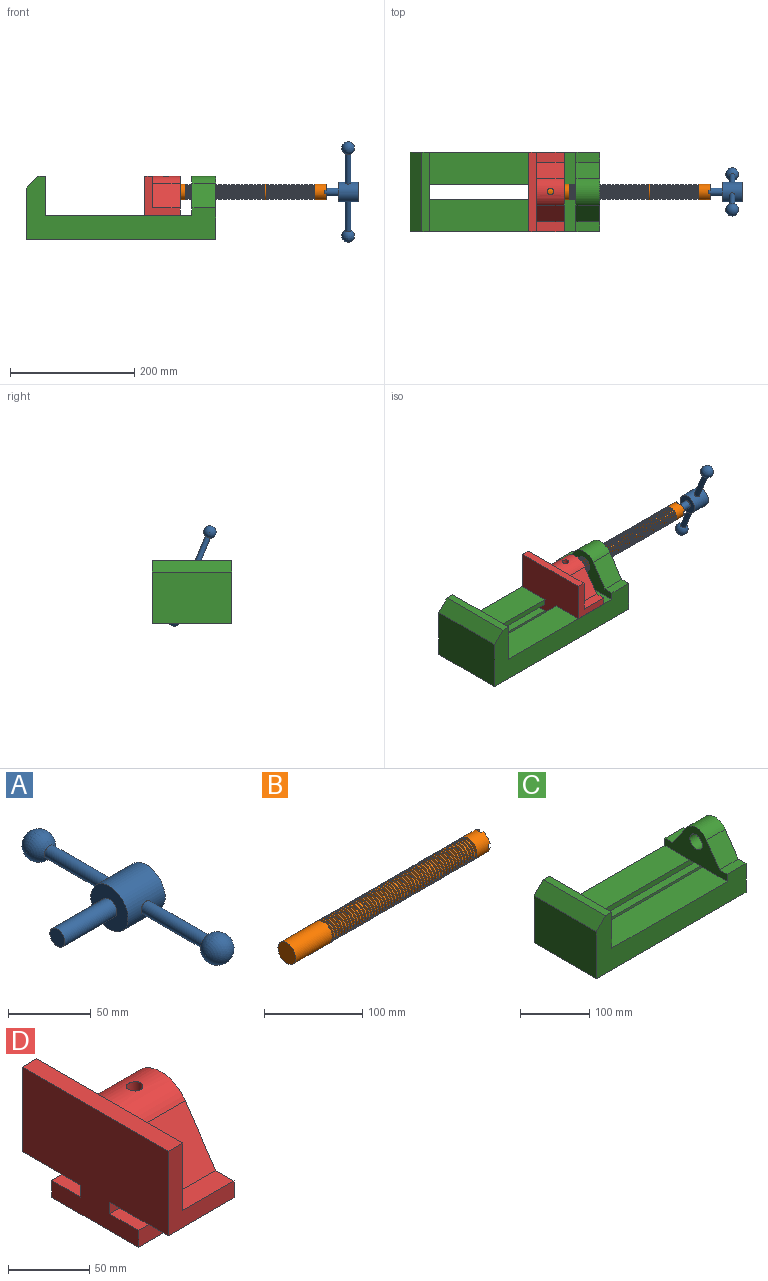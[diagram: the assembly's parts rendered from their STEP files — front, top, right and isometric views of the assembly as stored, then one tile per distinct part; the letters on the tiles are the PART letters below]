
ASSEMBLY  parts=4 mates=3
PART A: 13 faces, bbox 76.2x172.7x31.8 mm
  f0: cylinder r=4.45mm len=51.82mm, axis (0,1,0), area 1438.5mm2, adj f1,f8
  f1: cylinder r=15.88mm len=31.75mm, axis (-1,0,0), area 3041.6mm2, adj f0,f4,f5,f6
  f2: cylinder r=6.35mm len=44.45mm, axis (-1,0,0), area 1773.5mm2, adj f3,f5
  f3: plane 12.7x12.7mm, normal (-1,0,0), area 126.7mm2, adj f2
  f4: plane 31.75x31.75mm, normal (1,0,0), area 791.7mm2, adj f1
  f5: plane 31.75x31.75mm, normal (-1,0,0), area 665.1mm2, adj f1,f2
  f6: cylinder r=4.45mm len=51.82mm, axis (0,1,0), area 1438.5mm2, adj f1,f7
  f7: sphere r=10.16mm, area 1231.8mm2, adj f6
  f8: sphere r=10.16mm, area 1231.8mm2, adj f0
  f9: sphere r=4.45mm, area 124.1mm2, adj f10
  f10: plane 8.89x8.89mm, normal (0,-1,0), area 62.1mm2, adj f9
  f11: sphere r=4.45mm, area 124.1mm2, adj f12
  f12: plane 8.89x8.89mm, normal (0,1,0), area 62.1mm2, adj f11
PART B: 220 faces, bbox 279.4x25.4x25.4 mm
  f0: cylinder r=12.7mm len=25.4mm, axis (-1,0,0), area 1468.2mm2, adj f1,f2,f3,f4,f7,f208,f209,f210
  f1: plane 9.9x9.9mm, normal (1,0,0), area 62.3mm2, adj f0,f5,f215,f217
  f2: plane 9.9x9.9mm, normal (1,0,0), area 62.3mm2, adj f0,f5,f209,f218
  f3: plane 9.9x9.9mm, normal (1,0,0), area 62.3mm2, adj f0,f5,f211,f214
  f4: plane 9.9x9.9mm, normal (1,0,0), area 62.3mm2, adj f0,f5,f208,f212
  f5: cylinder r=6.35mm len=25.4mm, axis (1,0,0), area 960.3mm2, adj f1,f2,f3,f4,f6,f208,f209,f210
  f6: plane 12.7x12.7mm, normal (1,0,0), area 126.7mm2, adj f5
  f7: cone r=12.7mm half-angle=76deg, axis (1,0,0), area 188mm2, adj f0,f9
  f8: cone r=12.7mm half-angle=76deg, axis (-1,0,0), area 188mm2, adj f9,f10
  f9: cylinder r=10.16mm len=20.32mm, axis (1,0,0), area 81.1mm2, adj f7,f8
  f10: cylinder r=12.7mm len=25.4mm, axis (-1,0,0), area 131.7mm2, adj f8,f11
  f11: cone r=12.7mm half-angle=76deg, axis (1,0,0), area 188mm2, adj f10,f13
  f12: cone r=12.7mm half-angle=76deg, axis (-1,0,0), area 188mm2, adj f13,f14
  f13: cylinder r=10.16mm len=20.32mm, axis (1,0,0), area 81.1mm2, adj f11,f12
  f14: cylinder r=12.7mm len=25.4mm, axis (-1,0,0), area 131.7mm2, adj f12,f15
  f15: cone r=12.7mm half-angle=76deg, axis (1,0,0), area 188mm2, adj f14,f17
  f16: cone r=12.7mm half-angle=76deg, axis (-1,0,0), area 188mm2, adj f17,f18
  f17: cylinder r=10.16mm len=20.32mm, axis (1,0,0), area 81.1mm2, adj f15,f16
  f18: cylinder r=12.7mm len=25.4mm, axis (-1,0,0), area 131.7mm2, adj f16,f19
  f19: cone r=12.7mm half-angle=76deg, axis (1,0,0), area 188mm2, adj f18,f21
  f20: cone r=12.7mm half-angle=76deg, axis (-1,0,0), area 188mm2, adj f21,f22
  f21: cylinder r=10.16mm len=20.32mm, axis (1,0,0), area 81.1mm2, adj f19,f20
  f22: cylinder r=12.7mm len=25.4mm, axis (-1,0,0), area 131.7mm2, adj f20,f23
  f23: cone r=12.7mm half-angle=76deg, axis (1,0,0), area 188mm2, adj f22,f25
  f24: cone r=12.7mm half-angle=76deg, axis (-1,0,0), area 188mm2, adj f25,f26
  f25: cylinder r=10.16mm len=20.32mm, axis (1,0,0), area 81.1mm2, adj f23,f24
  f26: cylinder r=12.7mm len=25.4mm, axis (-1,0,0), area 131.7mm2, adj f24,f27
  f27: cone r=12.7mm half-angle=76deg, axis (1,0,0), area 188mm2, adj f26,f29
  f28: cone r=12.7mm half-angle=76deg, axis (-1,0,0), area 188mm2, adj f29,f30
  f29: cylinder r=10.16mm len=20.32mm, axis (1,0,0), area 81.1mm2, adj f27,f28
  f30: cylinder r=12.7mm len=25.4mm, axis (-1,0,0), area 131.7mm2, adj f28,f31
  f31: cone r=12.7mm half-angle=76deg, axis (1,0,0), area 188mm2, adj f30,f33
  f32: cone r=12.7mm half-angle=76deg, axis (-1,0,0), area 188mm2, adj f33,f34
  f33: cylinder r=10.16mm len=20.32mm, axis (1,0,0), area 81.1mm2, adj f31,f32
  f34: cylinder r=12.7mm len=25.4mm, axis (-1,0,0), area 131.7mm2, adj f32,f35
  f35: cone r=12.7mm half-angle=76deg, axis (1,0,0), area 188mm2, adj f34,f37
  f36: cone r=12.7mm half-angle=76deg, axis (-1,0,0), area 188mm2, adj f37,f38
  f37: cylinder r=10.16mm len=20.32mm, axis (1,0,0), area 81.1mm2, adj f35,f36
  f38: cylinder r=12.7mm len=25.4mm, axis (-1,0,0), area 131.7mm2, adj f36,f39
  f39: cone r=12.7mm half-angle=76deg, axis (1,0,0), area 188mm2, adj f38,f41
  f40: cone r=12.7mm half-angle=76deg, axis (-1,0,0), area 188mm2, adj f41,f42
  f41: cylinder r=10.16mm len=20.32mm, axis (1,0,0), area 81.1mm2, adj f39,f40
  f42: cylinder r=12.7mm len=25.4mm, axis (-1,0,0), area 131.7mm2, adj f40,f43
  f43: cone r=12.7mm half-angle=76deg, axis (1,0,0), area 188mm2, adj f42,f45
  f44: cone r=12.7mm half-angle=76deg, axis (-1,0,0), area 188mm2, adj f45,f46
  f45: cylinder r=10.16mm len=20.32mm, axis (1,0,0), area 81.1mm2, adj f43,f44
  f46: cylinder r=12.7mm len=25.4mm, axis (-1,0,0), area 131.7mm2, adj f44,f47
  f47: cone r=12.7mm half-angle=76deg, axis (1,0,0), area 188mm2, adj f46,f49
  f48: cone r=12.7mm half-angle=76deg, axis (-1,0,0), area 188mm2, adj f49,f50
  f49: cylinder r=10.16mm len=20.32mm, axis (1,0,0), area 81.1mm2, adj f47,f48
  f50: cylinder r=12.7mm len=25.4mm, axis (-1,0,0), area 131.7mm2, adj f48,f51
  f51: cone r=12.7mm half-angle=76deg, axis (1,0,0), area 188mm2, adj f50,f53
  f52: cone r=12.7mm half-angle=76deg, axis (-1,0,0), area 188mm2, adj f53,f54
  f53: cylinder r=10.16mm len=20.32mm, axis (1,0,0), area 81.1mm2, adj f51,f52
  f54: cylinder r=12.7mm len=25.4mm, axis (-1,0,0), area 131.7mm2, adj f52,f55
  f55: cone r=12.7mm half-angle=76deg, axis (1,0,0), area 188mm2, adj f54,f57
  f56: cone r=12.7mm half-angle=76deg, axis (-1,0,0), area 188mm2, adj f57,f58
  f57: cylinder r=10.16mm len=20.32mm, axis (1,0,0), area 81.1mm2, adj f55,f56
  f58: cylinder r=12.7mm len=25.4mm, axis (-1,0,0), area 131.7mm2, adj f56,f59
  f59: cone r=12.7mm half-angle=76deg, axis (1,0,0), area 188mm2, adj f58,f61
  f60: cone r=12.7mm half-angle=76deg, axis (-1,0,0), area 188mm2, adj f61,f62
  f61: cylinder r=10.16mm len=20.32mm, axis (1,0,0), area 81.1mm2, adj f59,f60
  f62: cylinder r=12.7mm len=25.4mm, axis (-1,0,0), area 131.7mm2, adj f60,f63
  f63: cone r=12.7mm half-angle=76deg, axis (1,0,0), area 188mm2, adj f62,f65
  f64: cone r=12.7mm half-angle=76deg, axis (-1,0,0), area 188mm2, adj f65,f66
  f65: cylinder r=10.16mm len=20.32mm, axis (1,0,0), area 81.1mm2, adj f63,f64
  f66: cylinder r=12.7mm len=25.4mm, axis (-1,0,0), area 131.7mm2, adj f64,f67
  f67: cone r=12.7mm half-angle=76deg, axis (1,0,0), area 188mm2, adj f66,f69
  f68: cone r=12.7mm half-angle=76deg, axis (-1,0,0), area 188mm2, adj f69,f70
  f69: cylinder r=10.16mm len=20.32mm, axis (1,0,0), area 81.1mm2, adj f67,f68
  f70: cylinder r=12.7mm len=25.4mm, axis (-1,0,0), area 131.7mm2, adj f68,f71
  f71: cone r=12.7mm half-angle=76deg, axis (1,0,0), area 188mm2, adj f70,f73
  f72: cone r=12.7mm half-angle=76deg, axis (-1,0,0), area 188mm2, adj f73,f74
  f73: cylinder r=10.16mm len=20.32mm, axis (1,0,0), area 81.1mm2, adj f71,f72
  f74: cylinder r=12.7mm len=25.4mm, axis (-1,0,0), area 131.7mm2, adj f72,f75
  f75: cone r=12.7mm half-angle=76deg, axis (1,0,0), area 188mm2, adj f74,f77
  f76: cone r=12.7mm half-angle=76deg, axis (-1,0,0), area 188mm2, adj f77,f78
  f77: cylinder r=10.16mm len=20.32mm, axis (1,0,0), area 81.1mm2, adj f75,f76
  f78: cylinder r=12.7mm len=25.4mm, axis (-1,0,0), area 131.7mm2, adj f76,f79
  f79: cone r=12.7mm half-angle=76deg, axis (1,0,0), area 188mm2, adj f78,f81
  f80: cone r=12.7mm half-angle=76deg, axis (-1,0,0), area 188mm2, adj f81,f82
  f81: cylinder r=10.16mm len=20.32mm, axis (1,0,0), area 81.1mm2, adj f79,f80
  f82: cylinder r=12.7mm len=25.4mm, axis (-1,0,0), area 131.7mm2, adj f80,f83
  f83: cone r=12.7mm half-angle=76deg, axis (1,0,0), area 188mm2, adj f82,f85
  f84: cone r=12.7mm half-angle=76deg, axis (-1,0,0), area 188mm2, adj f85,f86
  f85: cylinder r=10.16mm len=20.32mm, axis (1,0,0), area 81.1mm2, adj f83,f84
  f86: cylinder r=12.7mm len=25.4mm, axis (-1,0,0), area 131.7mm2, adj f84,f87
  f87: cone r=12.7mm half-angle=76deg, axis (1,0,0), area 188mm2, adj f86,f89
  f88: cone r=12.7mm half-angle=76deg, axis (-1,0,0), area 188mm2, adj f89,f90
  f89: cylinder r=10.16mm len=20.32mm, axis (1,0,0), area 81.1mm2, adj f87,f88
  f90: cylinder r=12.7mm len=25.4mm, axis (-1,0,0), area 131.7mm2, adj f88,f91
  f91: cone r=12.7mm half-angle=76deg, axis (1,0,0), area 188mm2, adj f90,f93
  f92: cone r=12.7mm half-angle=76deg, axis (-1,0,0), area 188mm2, adj f93,f94
  f93: cylinder r=10.16mm len=20.32mm, axis (1,0,0), area 81.1mm2, adj f91,f92
  f94: cylinder r=12.7mm len=25.4mm, axis (-1,0,0), area 131.7mm2, adj f92,f95
  f95: cone r=12.7mm half-angle=76deg, axis (1,0,0), area 188mm2, adj f94,f97
  f96: cone r=12.7mm half-angle=76deg, axis (-1,0,0), area 188mm2, adj f97,f98
  f97: cylinder r=10.16mm len=20.32mm, axis (1,0,0), area 81.1mm2, adj f95,f96
  f98: cylinder r=12.7mm len=25.4mm, axis (-1,0,0), area 131.7mm2, adj f96,f99
  f99: cone r=12.7mm half-angle=76deg, axis (1,0,0), area 188mm2, adj f98,f101
  f100: cone r=12.7mm half-angle=76deg, axis (-1,0,0), area 188mm2, adj f101,f102
  f101: cylinder r=10.16mm len=20.32mm, axis (1,0,0), area 81.1mm2, adj f99,f100
  f102: cylinder r=12.7mm len=25.4mm, axis (-1,0,0), area 131.7mm2, adj f100,f103
  f103: cone r=12.7mm half-angle=76deg, axis (1,0,0), area 188mm2, adj f102,f105
  f104: cone r=12.7mm half-angle=76deg, axis (-1,0,0), area 188mm2, adj f105,f106
  f105: cylinder r=10.16mm len=20.32mm, axis (1,0,0), area 81.1mm2, adj f103,f104
  f106: cylinder r=12.7mm len=25.4mm, axis (-1,0,0), area 131.7mm2, adj f104,f107
  f107: cone r=12.7mm half-angle=76deg, axis (1,0,0), area 188mm2, adj f106,f109
  f108: cone r=12.7mm half-angle=76deg, axis (-1,0,0), area 188mm2, adj f109,f110
  f109: cylinder r=10.16mm len=20.32mm, axis (1,0,0), area 81.1mm2, adj f107,f108
  f110: cylinder r=12.7mm len=25.4mm, axis (-1,0,0), area 131.7mm2, adj f108,f111
  f111: cone r=12.7mm half-angle=76deg, axis (1,0,0), area 188mm2, adj f110,f113
  f112: cone r=12.7mm half-angle=76deg, axis (-1,0,0), area 188mm2, adj f113,f114
  f113: cylinder r=10.16mm len=20.32mm, axis (1,0,0), area 81.1mm2, adj f111,f112
  f114: cylinder r=12.7mm len=25.4mm, axis (-1,0,0), area 131.7mm2, adj f112,f115
  f115: cone r=12.7mm half-angle=76deg, axis (1,0,0), area 188mm2, adj f114,f117
  f116: cone r=12.7mm half-angle=76deg, axis (-1,0,0), area 188mm2, adj f117,f118
  f117: cylinder r=10.16mm len=20.32mm, axis (1,0,0), area 81.1mm2, adj f115,f116
  f118: cylinder r=12.7mm len=25.4mm, axis (-1,0,0), area 131.7mm2, adj f116,f119
  f119: cone r=12.7mm half-angle=76deg, axis (1,0,0), area 188mm2, adj f118,f121
  f120: cone r=12.7mm half-angle=76deg, axis (-1,0,0), area 188mm2, adj f121,f122
  f121: cylinder r=10.16mm len=20.32mm, axis (1,0,0), area 81.1mm2, adj f119,f120
  f122: cylinder r=12.7mm len=25.4mm, axis (-1,0,0), area 131.7mm2, adj f120,f123
  f123: cone r=12.7mm half-angle=76deg, axis (1,0,0), area 188mm2, adj f122,f125
  f124: cone r=12.7mm half-angle=76deg, axis (-1,0,0), area 188mm2, adj f125,f126
  f125: cylinder r=10.16mm len=20.32mm, axis (1,0,0), area 81.1mm2, adj f123,f124
  f126: cylinder r=12.7mm len=25.4mm, axis (-1,0,0), area 131.7mm2, adj f124,f127
  f127: cone r=12.7mm half-angle=76deg, axis (1,0,0), area 188mm2, adj f126,f129
  f128: cone r=12.7mm half-angle=76deg, axis (-1,0,0), area 188mm2, adj f129,f130
  f129: cylinder r=10.16mm len=20.32mm, axis (1,0,0), area 81.1mm2, adj f127,f128
  f130: cylinder r=12.7mm len=25.4mm, axis (-1,0,0), area 131.7mm2, adj f128,f131
  f131: cone r=12.7mm half-angle=76deg, axis (1,0,0), area 188mm2, adj f130,f133
  f132: cone r=12.7mm half-angle=76deg, axis (-1,0,0), area 188mm2, adj f133,f134
  f133: cylinder r=10.16mm len=20.32mm, axis (1,0,0), area 81.1mm2, adj f131,f132
  f134: cylinder r=12.7mm len=25.4mm, axis (-1,0,0), area 131.7mm2, adj f132,f135
  f135: cone r=12.7mm half-angle=76deg, axis (1,0,0), area 188mm2, adj f134,f137
  f136: cone r=12.7mm half-angle=76deg, axis (-1,0,0), area 188mm2, adj f137,f138
  f137: cylinder r=10.16mm len=20.32mm, axis (1,0,0), area 81.1mm2, adj f135,f136
  f138: cylinder r=12.7mm len=25.4mm, axis (-1,0,0), area 131.7mm2, adj f136,f139
  f139: cone r=12.7mm half-angle=76deg, axis (1,0,0), area 188mm2, adj f138,f141
  f140: cone r=12.7mm half-angle=76deg, axis (-1,0,0), area 188mm2, adj f141,f142
  f141: cylinder r=10.16mm len=20.32mm, axis (1,0,0), area 81.1mm2, adj f139,f140
  f142: cylinder r=12.7mm len=25.4mm, axis (-1,0,0), area 131.7mm2, adj f140,f143
  f143: cone r=12.7mm half-angle=76deg, axis (1,0,0), area 188mm2, adj f142,f145
  f144: cone r=12.7mm half-angle=76deg, axis (-1,0,0), area 188mm2, adj f145,f146
  f145: cylinder r=10.16mm len=20.32mm, axis (1,0,0), area 81.1mm2, adj f143,f144
  f146: cylinder r=12.7mm len=25.4mm, axis (-1,0,0), area 131.7mm2, adj f144,f147
  f147: cone r=12.7mm half-angle=76deg, axis (1,0,0), area 188mm2, adj f146,f149
  f148: cone r=12.7mm half-angle=76deg, axis (-1,0,0), area 188mm2, adj f149,f150
  f149: cylinder r=10.16mm len=20.32mm, axis (1,0,0), area 81.1mm2, adj f147,f148
  f150: cylinder r=12.7mm len=25.4mm, axis (-1,0,0), area 131.7mm2, adj f148,f151
  f151: cone r=12.7mm half-angle=76deg, axis (1,0,0), area 188mm2, adj f150,f153
  f152: cone r=12.7mm half-angle=76deg, axis (-1,0,0), area 188mm2, adj f153,f154
  f153: cylinder r=10.16mm len=20.32mm, axis (1,0,0), area 81.1mm2, adj f151,f152
  f154: cylinder r=12.7mm len=25.4mm, axis (-1,0,0), area 131.7mm2, adj f152,f155
  f155: cone r=12.7mm half-angle=76deg, axis (1,0,0), area 188mm2, adj f154,f157
  f156: cone r=12.7mm half-angle=76deg, axis (-1,0,0), area 188mm2, adj f157,f158
  f157: cylinder r=10.16mm len=20.32mm, axis (1,0,0), area 81.1mm2, adj f155,f156
  f158: cylinder r=12.7mm len=25.4mm, axis (-1,0,0), area 131.7mm2, adj f156,f159
  f159: cone r=12.7mm half-angle=76deg, axis (1,0,0), area 188mm2, adj f158,f161
  f160: cone r=12.7mm half-angle=76deg, axis (-1,0,0), area 188mm2, adj f161,f162
  f161: cylinder r=10.16mm len=20.32mm, axis (1,0,0), area 81.1mm2, adj f159,f160
  f162: cylinder r=12.7mm len=25.4mm, axis (-1,0,0), area 131.7mm2, adj f160,f163
  f163: cone r=12.7mm half-angle=76deg, axis (1,0,0), area 188mm2, adj f162,f165
  f164: cone r=12.7mm half-angle=76deg, axis (-1,0,0), area 188mm2, adj f165,f166
  f165: cylinder r=10.16mm len=20.32mm, axis (1,0,0), area 81.1mm2, adj f163,f164
  f166: cylinder r=12.7mm len=25.4mm, axis (-1,0,0), area 131.7mm2, adj f164,f167
  f167: cone r=12.7mm half-angle=76deg, axis (1,0,0), area 188mm2, adj f166,f169
  f168: cone r=12.7mm half-angle=76deg, axis (-1,0,0), area 188mm2, adj f169,f170
  f169: cylinder r=10.16mm len=20.32mm, axis (1,0,0), area 81.1mm2, adj f167,f168
  f170: cylinder r=12.7mm len=25.4mm, axis (-1,0,0), area 131.7mm2, adj f168,f171
  f171: cone r=12.7mm half-angle=76deg, axis (1,0,0), area 188mm2, adj f170,f173
  f172: cone r=12.7mm half-angle=76deg, axis (-1,0,0), area 188mm2, adj f173,f174
  f173: cylinder r=10.16mm len=20.32mm, axis (1,0,0), area 81.1mm2, adj f171,f172
  f174: cylinder r=12.7mm len=25.4mm, axis (-1,0,0), area 131.7mm2, adj f172,f175
  f175: cone r=12.7mm half-angle=76deg, axis (1,0,0), area 188mm2, adj f174,f177
  f176: cone r=12.7mm half-angle=76deg, axis (-1,0,0), area 188mm2, adj f177,f178
  f177: cylinder r=10.16mm len=20.32mm, axis (1,0,0), area 81.1mm2, adj f175,f176
  f178: cylinder r=12.7mm len=25.4mm, axis (-1,0,0), area 131.7mm2, adj f176,f179
  f179: cone r=12.7mm half-angle=76deg, axis (1,0,0), area 188mm2, adj f178,f181
  f180: cone r=12.7mm half-angle=76deg, axis (-1,0,0), area 188mm2, adj f181,f182
  f181: cylinder r=10.16mm len=20.32mm, axis (1,0,0), area 81.1mm2, adj f179,f180
  f182: cylinder r=12.7mm len=25.4mm, axis (-1,0,0), area 131.7mm2, adj f180,f183
  f183: cone r=12.7mm half-angle=76deg, axis (1,0,0), area 188mm2, adj f182,f185
  f184: cone r=12.7mm half-angle=76deg, axis (-1,0,0), area 188mm2, adj f185,f186
  f185: cylinder r=10.16mm len=20.32mm, axis (1,0,0), area 81.1mm2, adj f183,f184
  f186: cylinder r=12.7mm len=25.4mm, axis (-1,0,0), area 131.7mm2, adj f184,f187
  f187: cone r=12.7mm half-angle=76deg, axis (1,0,0), area 188mm2, adj f186,f189
  f188: cone r=12.7mm half-angle=76deg, axis (-1,0,0), area 188mm2, adj f189,f190
  f189: cylinder r=10.16mm len=20.32mm, axis (1,0,0), area 81.1mm2, adj f187,f188
  f190: cylinder r=12.7mm len=25.4mm, axis (-1,0,0), area 131.7mm2, adj f188,f191
  f191: cone r=12.7mm half-angle=76deg, axis (1,0,0), area 188mm2, adj f190,f193
  f192: cone r=12.7mm half-angle=76deg, axis (-1,0,0), area 188mm2, adj f193,f194
  f193: cylinder r=10.16mm len=20.32mm, axis (1,0,0), area 81.1mm2, adj f191,f192
  f194: cylinder r=12.7mm len=25.4mm, axis (-1,0,0), area 131.7mm2, adj f192,f195
  f195: cone r=12.7mm half-angle=76deg, axis (1,0,0), area 188mm2, adj f194,f197
  f196: cone r=12.7mm half-angle=76deg, axis (-1,0,0), area 188mm2, adj f197,f198
  f197: cylinder r=10.16mm len=20.32mm, axis (1,0,0), area 81.1mm2, adj f195,f196
  f198: cylinder r=12.7mm len=25.4mm, axis (-1,0,0), area 131.7mm2, adj f196,f199
  f199: cone r=12.7mm half-angle=76deg, axis (1,0,0), area 188mm2, adj f198,f201
  f200: cone r=12.7mm half-angle=76deg, axis (-1,0,0), area 188mm2, adj f201,f202
  f201: cylinder r=10.16mm len=20.32mm, axis (1,0,0), area 81.1mm2, adj f199,f200
  f202: cylinder r=12.7mm len=25.4mm, axis (-1,0,0), area 131.7mm2, adj f200,f203
  f203: cone r=12.7mm half-angle=76deg, axis (1,0,0), area 188mm2, adj f202,f205
  f204: cone r=12.7mm half-angle=76deg, axis (-1,0,0), area 188mm2, adj f205,f207
  f205: cylinder r=10.16mm len=20.32mm, axis (1,0,0), area 81.1mm2, adj f203,f204
  f206: plane 25.4x25.4mm, normal (-1,0,0), area 506.7mm2, adj f207
  f207: cylinder r=12.7mm len=52.45mm, axis (-1,0,0), area 4185.4mm2, adj f204,f206
  f208: plane 6.62x2.54mm, normal (0,0,1), area 16.8mm2, adj f0,f4,f5,f210
  f209: plane 6.62x2.54mm, normal (0,0,-1), area 16.8mm2, adj f0,f2,f5,f210
  f210: plane 6.88x5.08mm, normal (1,0,0), area 32.7mm2, adj f0,f5,f208,f209
  f211: plane 6.62x2.54mm, normal (0,-1,0), area 16.8mm2, adj f0,f3,f5,f213
  f212: plane 6.62x2.54mm, normal (0,1,0), area 16.8mm2, adj f0,f4,f5,f213
  f213: plane 6.88x5.08mm, normal (1,0,0), area 32.7mm2, adj f0,f5,f211,f212
  f214: plane 6.62x2.54mm, normal (0,0,1), area 16.8mm2, adj f0,f3,f5,f216
  f215: plane 6.62x2.54mm, normal (0,0,-1), area 16.8mm2, adj f0,f1,f5,f216
  f216: plane 6.88x5.08mm, normal (1,0,0), area 32.7mm2, adj f0,f5,f214,f215
  f217: plane 6.62x2.54mm, normal (0,-1,0), area 16.8mm2, adj f0,f1,f5,f219
  f218: plane 6.62x2.54mm, normal (0,1,0), area 16.8mm2, adj f0,f2,f5,f219
  f219: plane 6.88x5.08mm, normal (1,0,0), area 32.7mm2, adj f0,f5,f217,f218
PART C: 28 faces, bbox 304.8x127x101.6 mm
  f0: plane 234.95x50.8mm, normal (0,0,1), area 11935.5mm2, adj f5,f9,f16,f22
  f1: plane 234.95x50.8mm, normal (0,0,1), area 11935.5mm2, adj f5,f8,f16,f23
  f2: plane 127x82.55mm, normal (-1,0,0), area 10483.8mm2, adj f3,f7,f8,f9
  f3: plane 304.8x127mm, normal (0,0,-1), area 31774.1mm2, adj f2,f4,f5,f8,f9,f18,f27
  f4: plane 127x101.27mm, normal (1,0,0), area 7370.6mm2, adj f3,f8,f9,f10,f11,f12,f13,f14
  f5: plane 127x101.6mm, normal (1,0,0), area 9667.6mm2, adj f0,f1,f3,f6,f8,f9,f18,f19
  f6: plane 127x12.7mm, normal (0,0,1), area 1612.9mm2, adj f5,f7,f8,f9
  f7: plane 127x19.05mm, normal (-0.71,0,0.71), area 3421.5mm2, adj f2,f6,f8,f9
  f8: plane 304.8x101.6mm, normal (0,-1,0), area 13931.4mm2, adj f1,f2,f3,f4,f5,f6,f7,f14
  f9: plane 304.8x101.6mm, normal (0,1,0), area 13931.4mm2, adj f0,f2,f3,f4,f5,f6,f7,f10
  f10: plane 38.1x15.91mm, normal (0,0,1), area 606.2mm2, adj f4,f9,f11,f16
  f11: plane 39.29x38.1mm, normal (0,0.83,0.56), area 1807mm2, adj f4,f10,f12,f16
  f12: cylinder r=25.4mm len=42.08mm, axis (1,0,0), area 1889.1mm2, adj f4,f11,f13,f16
  f13: plane 39.31x38.1mm, normal (0,-0.83,0.56), area 1808.6mm2, adj f4,f12,f14,f16
  f14: plane 38.1x15.84mm, normal (0,0,1), area 603.5mm2, adj f4,f8,f13,f16
  f15: cylinder r=12.7mm len=38.1mm, axis (1,0,0), area 3040.2mm2, adj f4,f16
  f16: plane 127x63.17mm, normal (-1,0,0), area 4135mm2, adj f0,f1,f8,f9,f10,f11,f12,f13
  f17: plane 38.1x25.4mm, normal (0,0,-1), area 967.7mm2, adj f4,f16,f22,f23
  f18: plane 273.05x16.51mm, normal (0,-1,0), area 4508.1mm2, adj f3,f4,f5,f19
  f19: plane 273.05x25.02mm, normal (0,0,1), area 6830.5mm2, adj f4,f5,f18,f20
  f20: plane 273.05x12.7mm, normal (0,-1,0), area 3467.7mm2, adj f4,f5,f19,f21
  f21: plane 273.05x25.02mm, normal (0,0,-1), area 6830.5mm2, adj f4,f5,f20,f22
  f22: plane 273.05x8.89mm, normal (0,-1,0), area 2427.4mm2, adj f0,f4,f5,f17,f21
  f23: plane 273.05x8.89mm, normal (0,1,0), area 2427.4mm2, adj f1,f4,f5,f17,f24
  f24: plane 273.05x25.02mm, normal (0,0,-1), area 6830.5mm2, adj f4,f5,f23,f25
  f25: plane 273.05x12.7mm, normal (0,1,0), area 3467.7mm2, adj f4,f5,f24,f26
  f26: plane 273.05x25.02mm, normal (0,0,1), area 6830.5mm2, adj f4,f5,f25,f27
  f27: plane 273.05x16.51mm, normal (0,1,0), area 4508.1mm2, adj f3,f4,f5,f26
PART D: 23 faces, bbox 57.2x127x85.1 mm
  f0: plane 57.15x50.8mm, normal (0,0,-1), area 2903.2mm2, adj f3,f7,f8,f16
  f1: plane 44.45x15.91mm, normal (0,0,1), area 707.2mm2, adj f3,f5,f9,f11
  f2: plane 57.15x50.8mm, normal (0,0,-1), area 2903.2mm2, adj f3,f7,f9,f22
  f3: plane 127x84.76mm, normal (1,0,0), area 5318.8mm2, adj f0,f1,f2,f4,f8,f9,f10,f11
  f4: plane 44.45x15.84mm, normal (0,0,1), area 704mm2, adj f3,f5,f8,f10
  f5: plane 127x50.8mm, normal (1,0,0), area 3422.8mm2, adj f1,f4,f6,f8,f9,f10,f11,f13
  f6: plane 127x12.7mm, normal (0,0,1), area 1612.9mm2, adj f5,f7,f8,f9
  f7: plane 127x85.09mm, normal (-1,0,0), area 9248.3mm2, adj f0,f2,f6,f8,f9,f16,f17,f18
  f8: plane 63.5x57.15mm, normal (0,-1,0), area 1371mm2, adj f0,f3,f4,f5,f6,f7
  f9: plane 63.5x57.15mm, normal (0,1,0), area 1371mm2, adj f1,f2,f3,f5,f6,f7
  f10: plane 44.45x39.31mm, normal (0,-0.83,0.56), area 2110mm2, adj f3,f4,f5,f13
  f11: plane 44.45x39.29mm, normal (0,0.83,0.56), area 2108.2mm2, adj f1,f3,f5,f13
  f12: cylinder r=12.7mm len=44.45mm, axis (1,0,0), area 3463.8mm2, adj f3,f14,f15
  f13: cylinder r=25.4mm len=44.45mm, axis (1,0,0), area 2122.5mm2, adj f3,f5,f10,f11,f15
  f14: plane 25.4x25.4mm, normal (1,0,0), area 506.7mm2, adj f12
  f15: cylinder r=5.08mm len=13.76mm, axis (0,0,1), area 403.7mm2, adj f12,f13
  f16: plane 57.15x8.89mm, normal (0,-1,0), area 508.1mm2, adj f0,f3,f7,f17
  f17: plane 57.15x25.02mm, normal (0,0,1), area 1429.6mm2, adj f3,f7,f16,f18
  f18: plane 57.15x12.7mm, normal (0,-1,0), area 725.8mm2, adj f3,f7,f17,f19
  f19: plane 75.43x57.15mm, normal (0,0,-1), area 4310.9mm2, adj f3,f7,f18,f20
  f20: plane 57.15x12.7mm, normal (0,1,0), area 725.8mm2, adj f3,f7,f19,f21
  f21: plane 57.15x25.02mm, normal (0,0,1), area 1429.6mm2, adj f3,f7,f20,f22
  f22: plane 57.15x8.89mm, normal (0,1,0), area 508.1mm2, adj f2,f3,f7,f21
PLACE A rot(axis=(1,0,0),112.1deg) t=(155.76,70.6,104.87)mm
PLACE B t=(158.94,0,0)mm
PLACE C at identity fixed
PLACE D t=(158.94,0,0)mm
MATE revolute A.f2 <-> B.f5  axis (1,0,0) through (152.59,0,76.2)mm
MATE fastened D.f12 <-> B.f5  axis (1,0,0) through (-101.41,0,76.2)mm
MATE slider D.f7 <-> C.f5  axis (-1,0,0) through (-114.11,-63.5,38.1)mm
